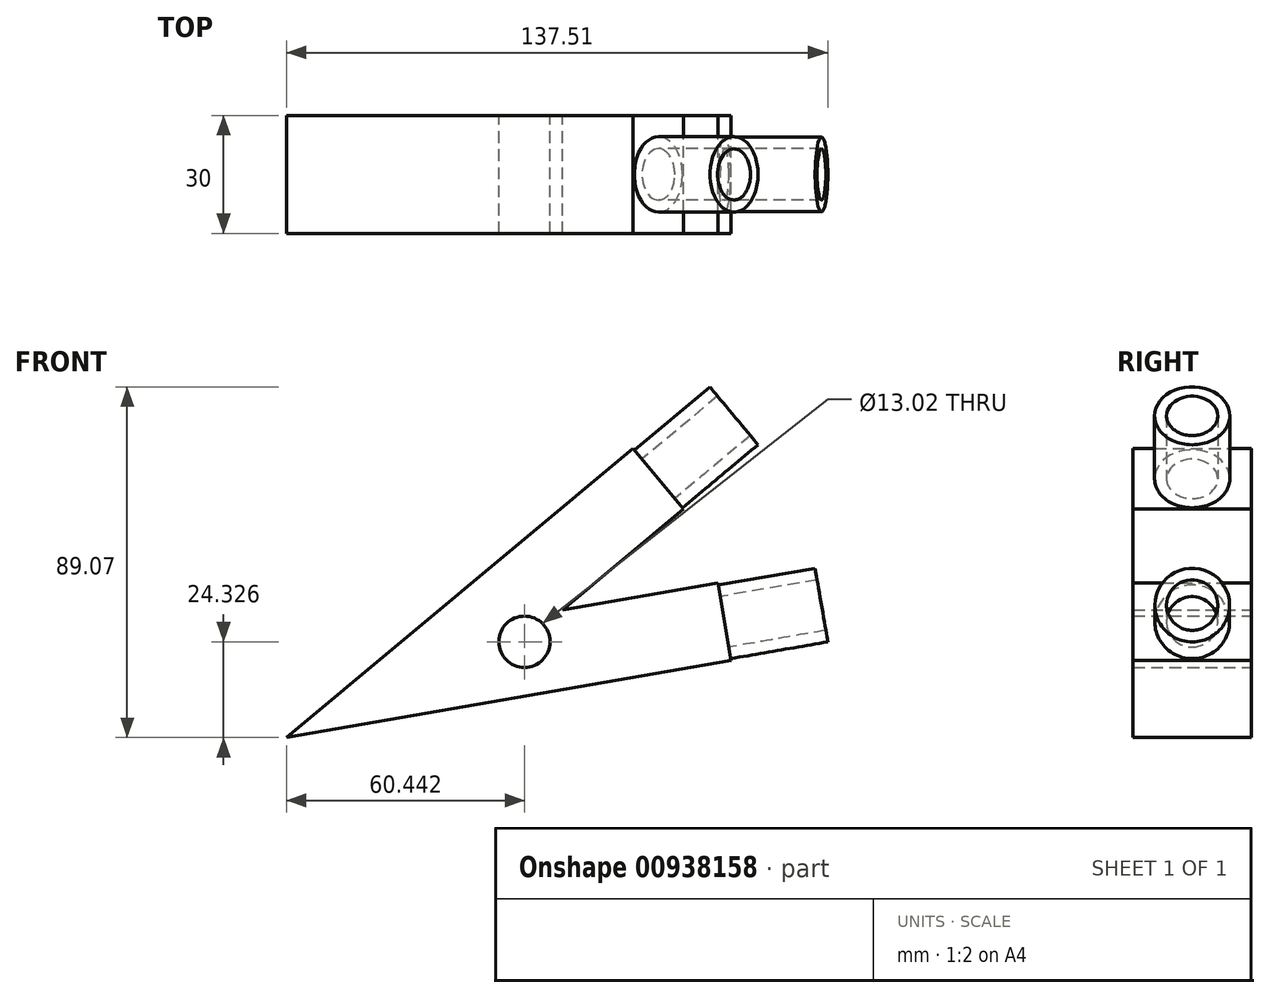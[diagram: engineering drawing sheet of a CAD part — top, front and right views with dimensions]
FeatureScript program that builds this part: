
annotation { "Feature Type Name" : "Feature", "Feature Type Description" : "" }
export const myFeature = defineFeature(function(context is Context, id is Id, definition is map)
    precondition{}
    {
        {
            var Q0;
            Q0=qCreatedBy(makeId("Front.planeOp"),FACE);
            var sketch = newSketch(context, id + "F0", { "sketchPlane" : qUnion([Q0])});
            skLineSegment(sketch, "E0", {"start": v(-40.07, -28.94) * mm, "end": v(-0.66, -22.12) * mm});
            skLineSegment(sketch, "E1", {"start": v(-40.07, -28.94) * mm, "end": v(-9.35, -3.33) * mm});
            skLineSegment(sketch, "E2", {"start": v(-0.66, -22.12) * mm, "end": v(2.75, -41.83) * mm});
            skLineSegment(sketch, "E3", {"start": v(2.75, -41.83) * mm, "end": v(-94.3, -58.62) * mm});
            skLineSegment(sketch, "E4", {"start": v(-9.35, -3.33) * mm, "end": v(-22.15, 12.03) * mm});
            skLineSegment(sketch, "E5", {"start": v(-22.15, 12.03) * mm, "end": v(-110.21, -61.37) * mm});
            skLineSegment(sketch, "E6", {"start": v(-94.3, -58.62) * mm, "end": v(-110.21, -61.37) * mm});
            skCircle(sketch, "E7", {"center": v(-49.77, -37.04) * mm, "radius": 6.5 * mm});
            skSolve(sketch);
        }
        {
            var Q0;
            Q0=makeQuery(id+"F0.imprint","IMPRINT",FACE,{"disambiguationData":[TD([[makeQuery(id+"F0.imprint","IMPRINT",EDGE,{"derivedFrom":sQuery(id+"F0.wireOp",EDGE,"E0")}),-1.0]])]});
            extrude(context, id + "F1", {"entities" : qUnion([Q0]), "depth" : 30 * mm, "offsetDistance" : 25 * mm});
        }
        {
            var Q0;
            Q0=makeQuery(id+"F1.opExtrude","SWEPT_FACE",FACE,{"disambiguationData":[OSD([sQuery(id+"F0.wireOp",EDGE,"E4")])]});
            var sketch = newSketch(context, id + "F2", { "sketchPlane" : qUnion([Q0])});
            skLineSegment(sketch, "E8", {"start": v(-30, 23.43) * mm, "end": v(0, 3.43) * mm, "construction": true});
            skLineSegment(sketch, "E9", {"start": v(0, 3.43) * mm, "end": v(0, 23.43) * mm, "construction": true});
            skLineSegment(sketch, "E10", {"start": v(0, 23.43) * mm, "end": v(-30, 3.43) * mm, "construction": true});
            skCircle(sketch, "E11", {"center": v(-15, 13.43) * mm, "radius": 8.22 * mm, "construction": true});
            skCircle(sketch, "E12", {"center": v(-15, 13.43) * mm, "radius": 9.56 * mm});
            skCircle(sketch, "E13", {"center": v(-15, 13.43) * mm, "radius": 6.5 * mm});
            skSolve(sketch);
        }
        {
            var Q0;
            Q0=makeQuery(id+"F1.opExtrude","SWEPT_FACE",FACE,{"disambiguationData":[OSD([sQuery(id+"F0.wireOp",EDGE,"E2")])]});
            var sketch = newSketch(context, id + "F3", { "sketchPlane" : qUnion([Q0])});
            skLineSegment(sketch, "E14", {"start": v(0, -21.69) * mm, "end": v(-30, -41.69) * mm, "construction": true});
            skLineSegment(sketch, "E15", {"start": v(-30, -41.69) * mm, "end": v(0, -41.69) * mm, "construction": true});
            skLineSegment(sketch, "E16", {"start": v(0, -41.69) * mm, "end": v(-30, -21.69) * mm, "construction": true});
            skCircle(sketch, "E17", {"center": v(-15, -31.69) * mm, "radius": 6.5 * mm});
            skCircle(sketch, "E18", {"center": v(-15, -31.69) * mm, "radius": 9.49 * mm});
            skSolve(sketch);
        }
        {
            var Q0;
            Q0=makeQuery(id+"F3.imprint","IMPRINT",FACE,{"disambiguationData":[TD([[makeQuery(id+"F3.imprint","IMPRINT",EDGE,{"derivedFrom":sQuery(id+"F3.wireOp",EDGE,"E17")}),-1.0]])]});
            extrude(context, id + "F4", {"entities" : qUnion([Q0]), "operationType" : NewBodyOperationType.ADD, "depth" : 25 * mm, "offsetDistance" : 25 * mm});
        }
        {
            var Q0;
            Q0=makeQuery(id+"F2.imprint","IMPRINT",FACE,{"disambiguationData":[TD([[makeQuery(id+"F2.imprint","IMPRINT",EDGE,{"derivedFrom":sQuery(id+"F2.wireOp",EDGE,"E12")}),1.0]])]});
            extrude(context, id + "F5", {"entities" : qUnion([Q0]), "operationType" : NewBodyOperationType.ADD, "depth" : 25 * mm, "offsetDistance" : 25 * mm});
        }
    });
